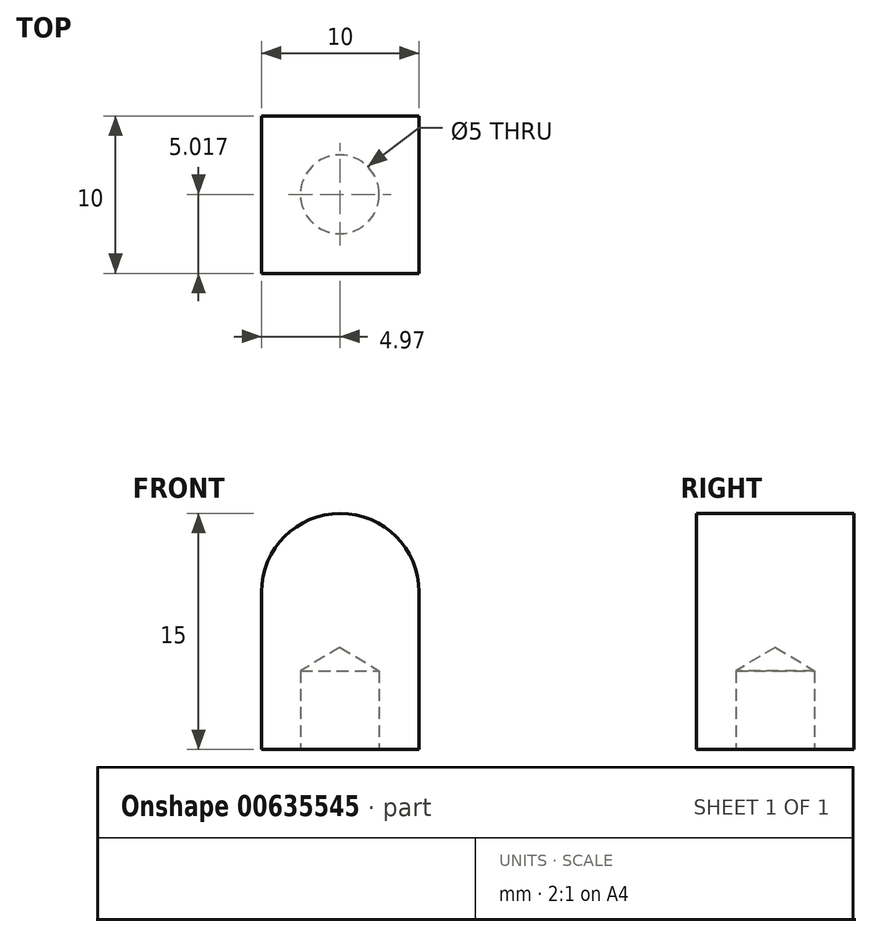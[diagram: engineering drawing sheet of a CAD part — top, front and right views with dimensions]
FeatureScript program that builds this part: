
annotation { "Feature Type Name" : "Feature", "Feature Type Description" : "" }
export const myFeature = defineFeature(function(context is Context, id is Id, definition is map)
    precondition{}
    {
        {
            var Q0;
            Q0=qCreatedBy(makeId("Front.planeOp"),FACE);
            var sketch = newSketch(context, id + "F0", { "sketchPlane" : qUnion([Q0])});
            skLineSegment(sketch, "E0.bottom", {"start": v(0, 0) * mm, "end": v(-10, 0) * mm});
            skLineSegment(sketch, "E0.top", {"start": v(0, 10) * mm, "end": v(-10, 10) * mm});
            skLineSegment(sketch, "E0.left", {"start": v(0, 0) * mm, "end": v(0, 10) * mm});
            skLineSegment(sketch, "E0.right", {"start": v(-10, 0) * mm, "end": v(-10, 10) * mm});
            skCircle(sketch, "E1", {"center": v(-5, 10) * mm, "radius": 5 * mm});
            skSolve(sketch);
        }
        {
            var Q0;
            Q0=makeQuery(id+"F0.imprint","IMPRINT",FACE,{"disambiguationData":[TD([[makeQuery(id+"F0.imprint","IMPRINT",EDGE,{"derivedFrom":sQuery(id+"F0.wireOp",EDGE,"E0.bottom")}),-1.0]])]});
            var Q1;
            {var subQ0=sQuery(id+"F0.wireOp",EDGE,"E0.top");Q1=makeQuery(id+"F0.imprint","IMPRINT",FACE,{"disambiguationData":[TD([[makeQuery(id+"F0.imprint","IMPRINT",EDGE,{"derivedFrom":subQ0}),-1.0]])]});}
            var Q2;
            {var subQ0=sQuery(id+"F0.wireOp",EDGE,"E0.top");Q2=makeQuery(id+"F0.imprint","IMPRINT",FACE,{"disambiguationData":[TD([[makeQuery(id+"F0.imprint","IMPRINT",EDGE,{"derivedFrom":subQ0}),1.0]])]});}
            extrude(context, id + "F1", {"entities" : qUnion([Q0, Q1, Q2]), "depth" : 10 * mm, "offsetDistance" : 25.4 * mm});
        }
        {
            var Q0;
            Q0=makeQuery(id+"F1.opExtrude","SWEPT_FACE",FACE,{"disambiguationData":[OSD([sQuery(id+"F0.wireOp",EDGE,"E0.bottom")])]});
            var sketch = newSketch(context, id + "F2", { "sketchPlane" : qUnion([Q0])});
            skLineSegment(sketch, "E2", {"start": v(-10, 5) * mm, "end": v(0, 5) * mm});
            skSolve(sketch);
        }
        {
            var Q0;
            {var subQ0=sQuery(id+"F2.wireOp",EDGE,"E2");Q0=makeQuery(id+"F2.imprint","IMPRINT",FACE,{"disambiguationData":[TD([[makeQuery(id+"F2.imprint","IMPRINT",EDGE,{"derivedFrom":subQ0}),1.0]])]});}
            var sketch = newSketch(context, id + "F3", { "sketchPlane" : qUnion([Q0])});
            skLineSegment(sketch, "E3", {"start": v(-5.03, 9.97) * mm, "end": v(-5.03, 0) * mm});
            skCircle(sketch, "E4", {"center": v(-5.03, 4.98) * mm, "radius": 1.8 * mm});
            skSolve(sketch);
        }
        {
            var Q0;
            Q0=sQuery(id+"F3.wireOp",VERTEX,"E4.center");
            var Q1;
            Q1=makeQuery(id+"F1.opExtrude","SWEPT_BODY",BODY,{"disambiguationData":[OSD([sQuery(id+"F0.wireOp",EDGE,"E0.bottom"),sQuery(id+"F0.wireOp",EDGE,"E0.left"),sQuery(id+"F0.wireOp",EDGE,"E0.right"),sQuery(id+"F0.wireOp",EDGE,"E1")])]});
            hole(context, id + "F4", {"style" : HoleStyle.SIMPLE, "endStyle" : HoleEndStyle.BLIND, "holeDiameter" : 5 * mm, "majorDiameter" : 6.35 * mm, "holeDepth" : 5 * mm, "isTappedThrough" : true, "tappedDepth" : 12.7 * mm, "tapClearance" : 3, "locations" : qUnion([Q0]), "scope" : qUnion([Q1])});
        }
    });
